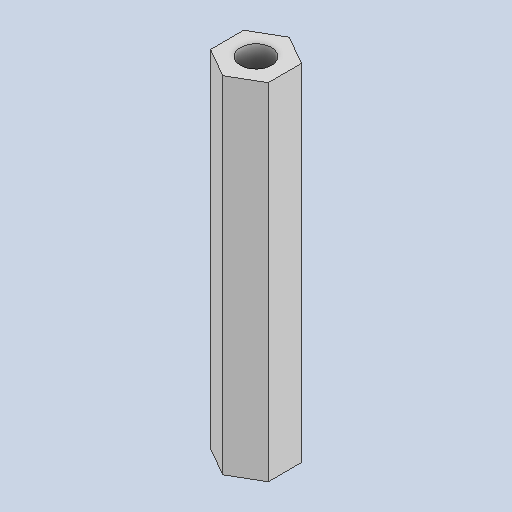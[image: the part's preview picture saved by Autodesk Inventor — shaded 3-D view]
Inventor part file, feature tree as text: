
AUTODESK INVENTOR PART (.ipt)
format: ipt  version: 2024 (Build 280153000, 153)  size: 89,600 bytes
history: native  units: in
note: dims shown in document units (in); Inventor stores cm internally (conversion verified against a paired STEP export)
features: extrude x1, sketch x1
ambient origin geometry x8: Origin, YZ Plane, XZ Plane, XY Plane, X Axis, Y Axis, Z Axis, Center Point
bodies: Solid1 (feature_tree)
feature tree (2):
  extrude  "Extrusion1"  Depth=1.5in
  sketch  "Sketch1"  dims[d0=0.25in d1=0.135in d3=1.5in d4=0.0in]
